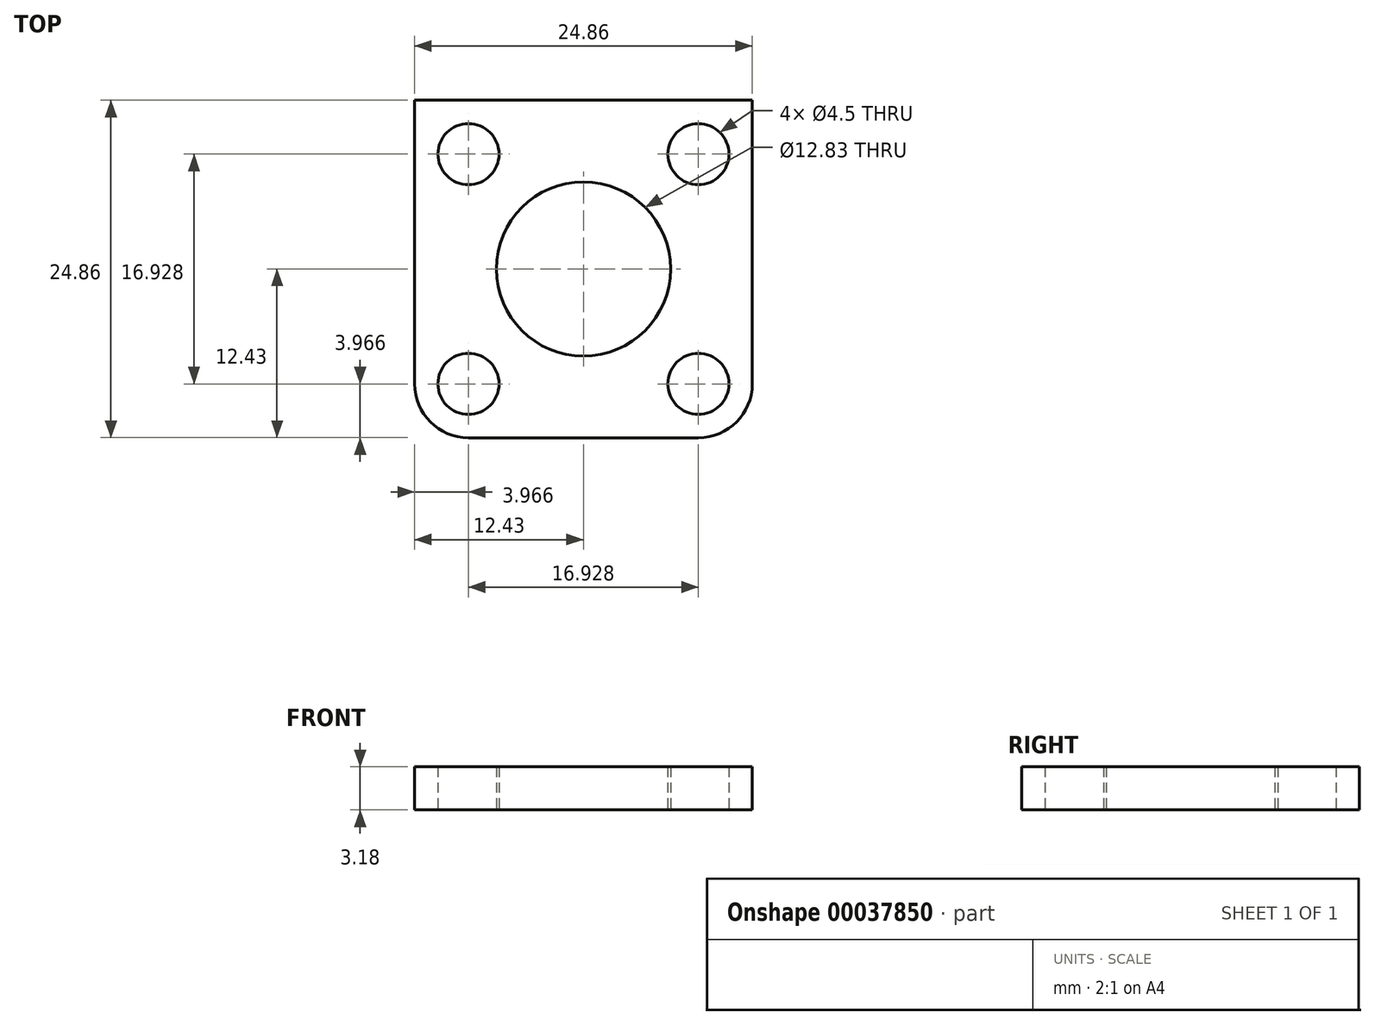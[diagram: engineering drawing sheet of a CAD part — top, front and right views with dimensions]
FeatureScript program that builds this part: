
annotation { "Feature Type Name" : "Feature", "Feature Type Description" : "" }
export const myFeature = defineFeature(function(context is Context, id is Id, definition is map)
    precondition{}
    {
        {
            var Q0;
            Q0=qCreatedBy(makeId("Top.planeOp"),FACE);
            var sketch = newSketch(context, id + "F0", { "sketchPlane" : qUnion([Q0])});
            skLineSegment(sketch, "E0.rect.bottom", {"start": v(12.43, -12.43) * mm, "end": v(-12.43, -12.43) * mm});
            skLineSegment(sketch, "E0.rect.top", {"start": v(12.43, 12.43) * mm, "end": v(-12.43, 12.43) * mm});
            skLineSegment(sketch, "E0.rect.left", {"start": v(12.43, -12.43) * mm, "end": v(12.43, 12.43) * mm});
            skLineSegment(sketch, "E0.rect.right", {"start": v(-12.43, -12.43) * mm, "end": v(-12.43, 12.43) * mm});
            skPoint(sketch, "E0.rect.middle", {"position": v(0, 0) * mm});
            skLineSegment(sketch, "E1.rect.bottom", {"start": v(8.46, -8.46) * mm, "end": v(-8.46, -8.46) * mm, "construction": true});
            skLineSegment(sketch, "E1.rect.top", {"start": v(8.46, 8.46) * mm, "end": v(-8.46, 8.46) * mm, "construction": true});
            skLineSegment(sketch, "E1.rect.left", {"start": v(8.46, -8.46) * mm, "end": v(8.46, 8.46) * mm, "construction": true});
            skLineSegment(sketch, "E1.rect.right", {"start": v(-8.46, -8.46) * mm, "end": v(-8.46, 8.46) * mm, "construction": true});
            skCircle(sketch, "E2", {"center": v(8.46, -8.46) * mm, "radius": 3.97 * mm, "construction": true});
            skCircle(sketch, "E3", {"center": v(0, 0) * mm, "radius": 6.41 * mm});
            skCircle(sketch, "E4", {"center": v(-8.46, -8.46) * mm, "radius": 2.25 * mm});
            skCircle(sketch, "E5", {"center": v(-8.46, 8.46) * mm, "radius": 2.25 * mm});
            skCircle(sketch, "E6", {"center": v(8.46, 8.46) * mm, "radius": 2.25 * mm});
            skCircle(sketch, "E7", {"center": v(8.46, -8.46) * mm, "radius": 2.25 * mm});
            skSolve(sketch);
        }
        {
            var Q0;
            Q0 = qSketchRegion(id + "F0", true);
            extrude(context, id + "F1", {"entities" : qUnion([Q0]), "depth" : 3.17 * mm});
        }
        {
            var Q0;
            Q0=makeQuery(id+"F1.opExtrude","SWEPT_EDGE",EDGE,{"disambiguationData":[OSD([sQuery(id+"F0.wireOp",EDGE,"E0.rect.bottom"),sQuery(id+"F0.wireOp",EDGE,"E0.rect.left")])]});
            var Q1;
            Q1=makeQuery(id+"F1.opExtrude","SWEPT_EDGE",EDGE,{"disambiguationData":[OSD([sQuery(id+"F0.wireOp",EDGE,"E0.rect.bottom"),sQuery(id+"F0.wireOp",EDGE,"E0.rect.right")])]});
            fillet(context, id + "F2", {"entities" : qUnion([Q0, Q1]), "radius" : 3.97 * mm, "tangentPropagation" : true, "allowEdgeOverflow" : false});
        }
    });
